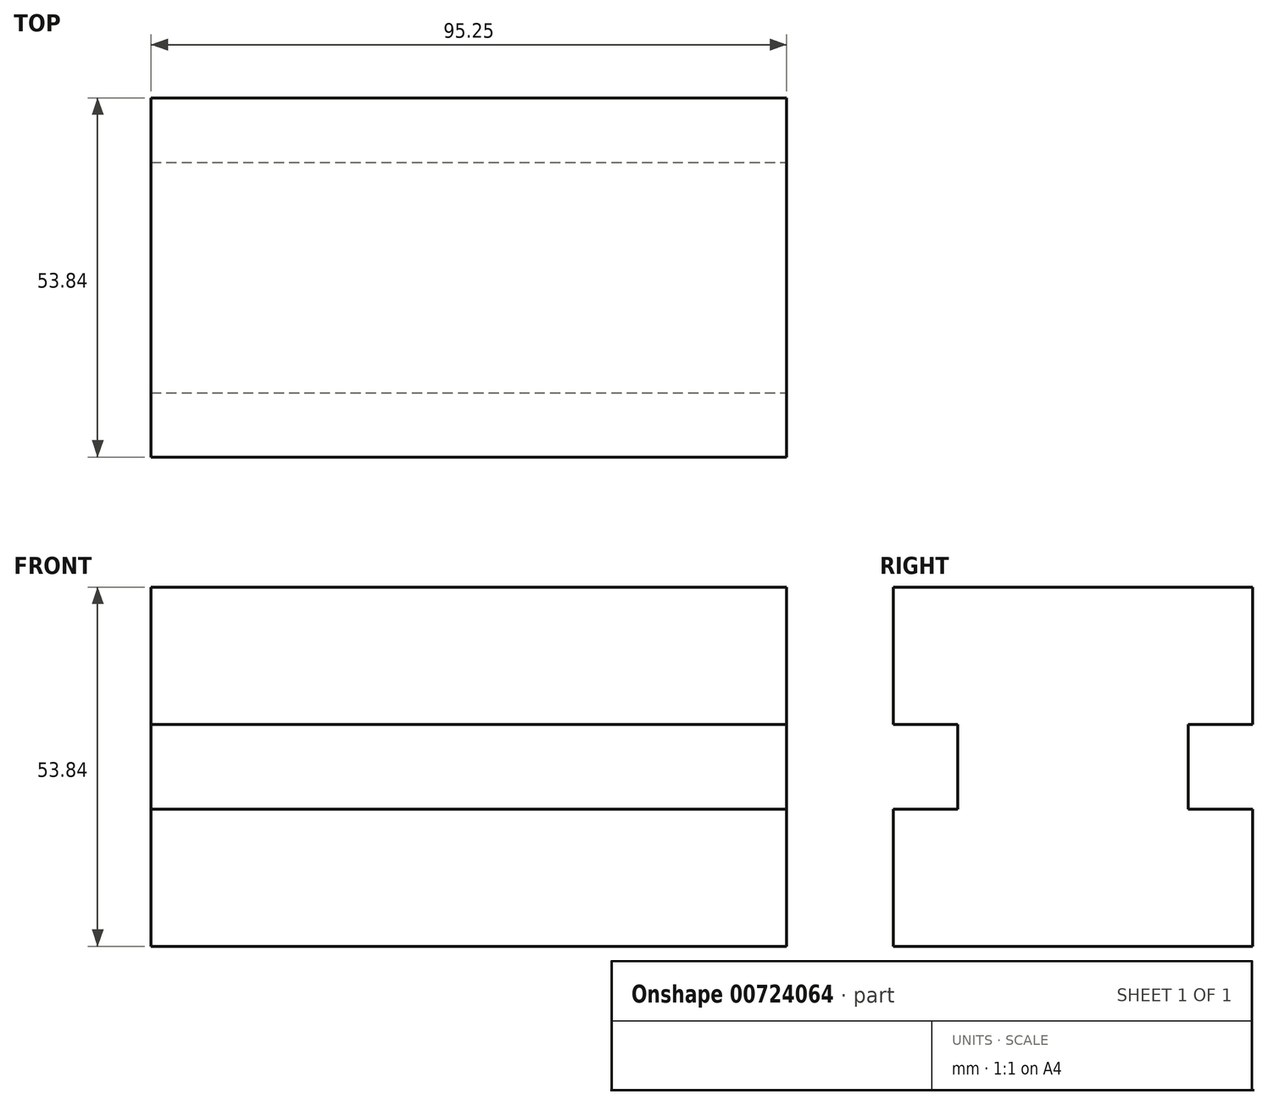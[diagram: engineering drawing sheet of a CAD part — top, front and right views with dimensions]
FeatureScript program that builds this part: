
annotation { "Feature Type Name" : "Feature", "Feature Type Description" : "" }
export const myFeature = defineFeature(function(context is Context, id is Id, definition is map)
    precondition{}
    {
        {
            var Q0;
            Q0=qCreatedBy(makeId("Right.planeOp"),FACE);
            var sketch = newSketch(context, id + "F0", { "sketchPlane" : qUnion([Q0])});
            skLineSegment(sketch, "E0.bottom", {"start": v(26.92, -26.92) * mm, "end": v(-26.92, -26.92) * mm});
            skLineSegment(sketch, "E0.top", {"start": v(26.92, 26.92) * mm, "end": v(-26.92, 26.92) * mm});
            skLineSegment(sketch, "E0.left", {"start": v(26.92, -26.92) * mm, "end": v(26.92, -6.35) * mm});
            skLineSegment(sketch, "E0.right", {"start": v(-26.92, -26.92) * mm, "end": v(-26.92, -6.35) * mm});
            skPoint(sketch, "E0.middle", {"position": v(0, 0) * mm});
            skLineSegment(sketch, "E1.bottom", {"start": v(-26.92, 6.35) * mm, "end": v(-17.27, 6.35) * mm});
            skLineSegment(sketch, "E1.top", {"start": v(-26.92, -6.35) * mm, "end": v(-17.27, -6.35) * mm});
            skLineSegment(sketch, "E1.right", {"start": v(-17.27, 6.35) * mm, "end": v(-17.27, -6.35) * mm});
            skLineSegment(sketch, "E2.trimOffspring", {"start": v(-26.92, 6.35) * mm, "end": v(-26.92, 26.92) * mm});
            skLineSegment(sketch, "E3", {"start": v(0, 47.33) * mm, "end": v(0, -50.82) * mm, "construction": true});
            skPoint(sketch, "E3.startSnap0", {"position": v(0, 26.92) * mm});
            skLineSegment(sketch, "E4.MirrorCS", {"start": v(26.92, 6.35) * mm, "end": v(17.27, 6.35) * mm});
            skLineSegment(sketch, "E5.MirrorCS", {"start": v(17.27, 6.35) * mm, "end": v(17.27, -6.35) * mm});
            skLineSegment(sketch, "E6.MirrorCS", {"start": v(26.92, -6.35) * mm, "end": v(17.27, -6.35) * mm});
            skLineSegment(sketch, "E7.trimOffspring", {"start": v(26.92, 6.35) * mm, "end": v(26.92, 26.92) * mm});
            skSolve(sketch);
        }
        {
            var Q0;
            Q0=makeQuery(id+"F0.imprint","IMPRINT",FACE,{"disambiguationData":[TD([[makeQuery(id+"F0.imprint","IMPRINT",EDGE,{"derivedFrom":sQuery(id+"F0.wireOp",EDGE,"E0.bottom")}),-1.0]])]});
            extrude(context, id + "F1", {"entities" : qUnion([Q0]), "oppositeDirection" : true, "depth" : 95.25 * mm, "offsetDistance" : 25.4 * mm});
        }
    });
